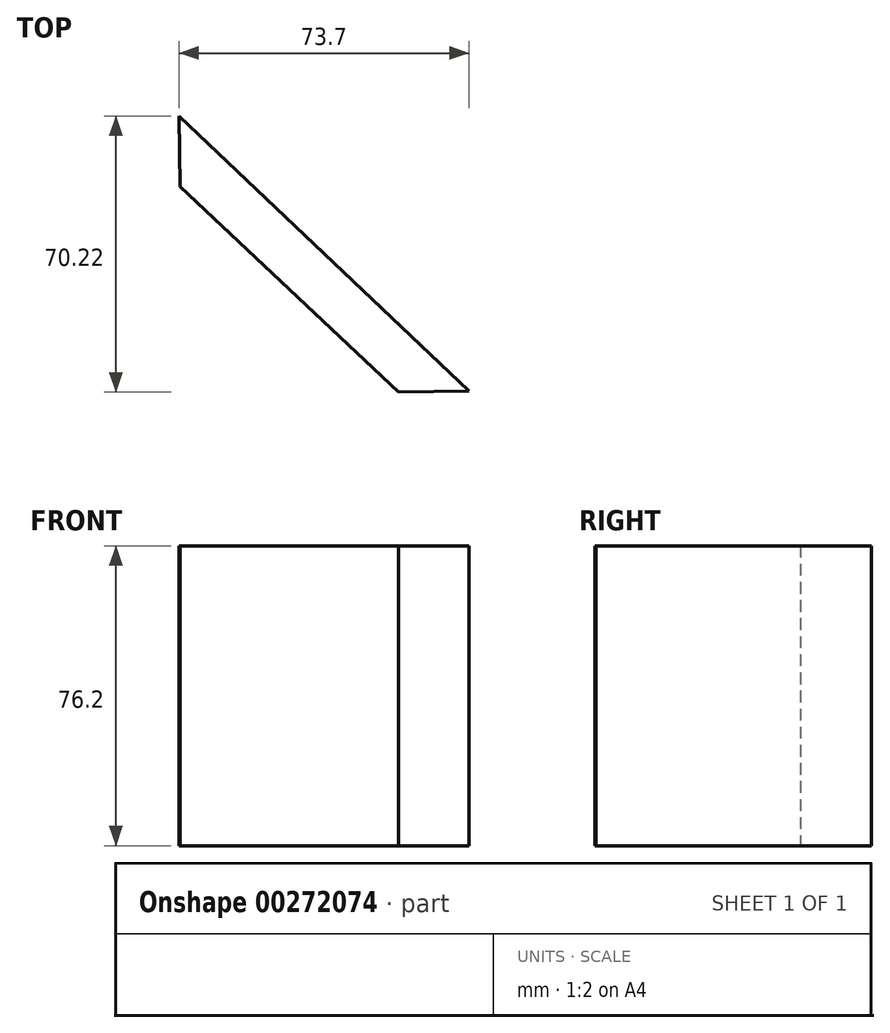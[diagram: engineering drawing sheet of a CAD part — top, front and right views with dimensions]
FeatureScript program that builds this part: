
annotation { "Feature Type Name" : "Feature", "Feature Type Description" : "" }
export const myFeature = defineFeature(function(context is Context, id is Id, definition is map)
    precondition{}
    {
        {
            var Q0;
            Q0=qCreatedBy(makeId("Top.planeOp"),FACE);
            var sketch = newSketch(context, id + "F0", { "sketchPlane" : qUnion([Q0])});
            skLineSegment(sketch, "E0", {"start": v(-62.96, 20.86) * mm, "end": v(-7.51, -31.41) * mm});
            skLineSegment(sketch, "E1", {"start": v(-63.26, 38.81) * mm, "end": v(10.44, -31.11) * mm});
            skLineSegment(sketch, "E2", {"start": v(-7.51, -31.41) * mm, "end": v(10.44, -31.11) * mm});
            skLineSegment(sketch, "E3", {"start": v(-63.26, 38.81) * mm, "end": v(-62.96, 20.86) * mm});
            skSolve(sketch);
        }
        {
            var Q0;
            Q0=makeQuery(id+"F0.imprint","IMPRINT",FACE,{"disambiguationData":[TD([[makeQuery(id+"F0.imprint","IMPRINT",EDGE,{"derivedFrom":sQuery(id+"F0.wireOp",EDGE,"E0")}),1.0]])]});
            extrude(context, id + "F1", {"entities" : qUnion([Q0]), "depth" : 76.2 * mm});
        }
    });
